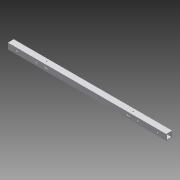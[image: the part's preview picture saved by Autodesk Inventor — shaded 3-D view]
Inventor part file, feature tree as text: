
AUTODESK INVENTOR PART (.ipt)
format: ipt  version: 2015 SP1 (Build 190203100, 203)  size: 147,456 bytes
history: native  units: in
note: dims shown in document units (in); Inventor stores cm internally (conversion verified against a paired STEP export)
features: sketch x4, extrude x2, hole x2
ambient origin geometry x8: Origin, YZ Plane, XZ Plane, XY Plane, X Axis, Y Axis, Z Axis, Center Point
bodies: Solid1 (feature_tree)
feature tree (8):
  extrude  "Extrusion1"  Depth=1.0in
  hole  "Hole2"  [1 undecoded]
  extrude  "Extrusion2"  Depth=0.125in
  hole  "Hole5"  [1 undecoded]
  sketch  "Sketch1"  dims[d0=1.0in d1=1.0in]
  sketch  "Sketch3"  dims[d2=0.75in d3=0.75in]
  sketch  "Sketch6"  dims[d4=0.125in d5=0.125in]
  sketch  "Sketch7"  dims[d6=27.0in d7=0.0in d23=1.5in d24=0.5in d25=0.5in d26=0.5in d27=4.875in d28=6.375in d29=0.5in d30=0.5in d31=0.5in d32=1.5in d33=4.875in d34=6.375in d35=0.25in d36=0.75in d37=0.375in d38=0.25in d39=0.5635in d40=1.0in d41=0.8108in d66=0.25in d67=0.25in d68=0.5in d69=0.25in d70=0.25in d71=0.5in d72=1.0in d73=0.0in d74=0.5in d75=0.5in d76=20.875in d77=6.125in d78=0.1875in d79=0.75in d80=0.375in d81=0.25in d82=0.5635in d83=1.0in d84=0.8108in]
note: 2 required parameter values undecoded (feature->parameter linkage not recoverable at this tier; creation-order binding heuristic only, values carry confidence <= 0.55)
